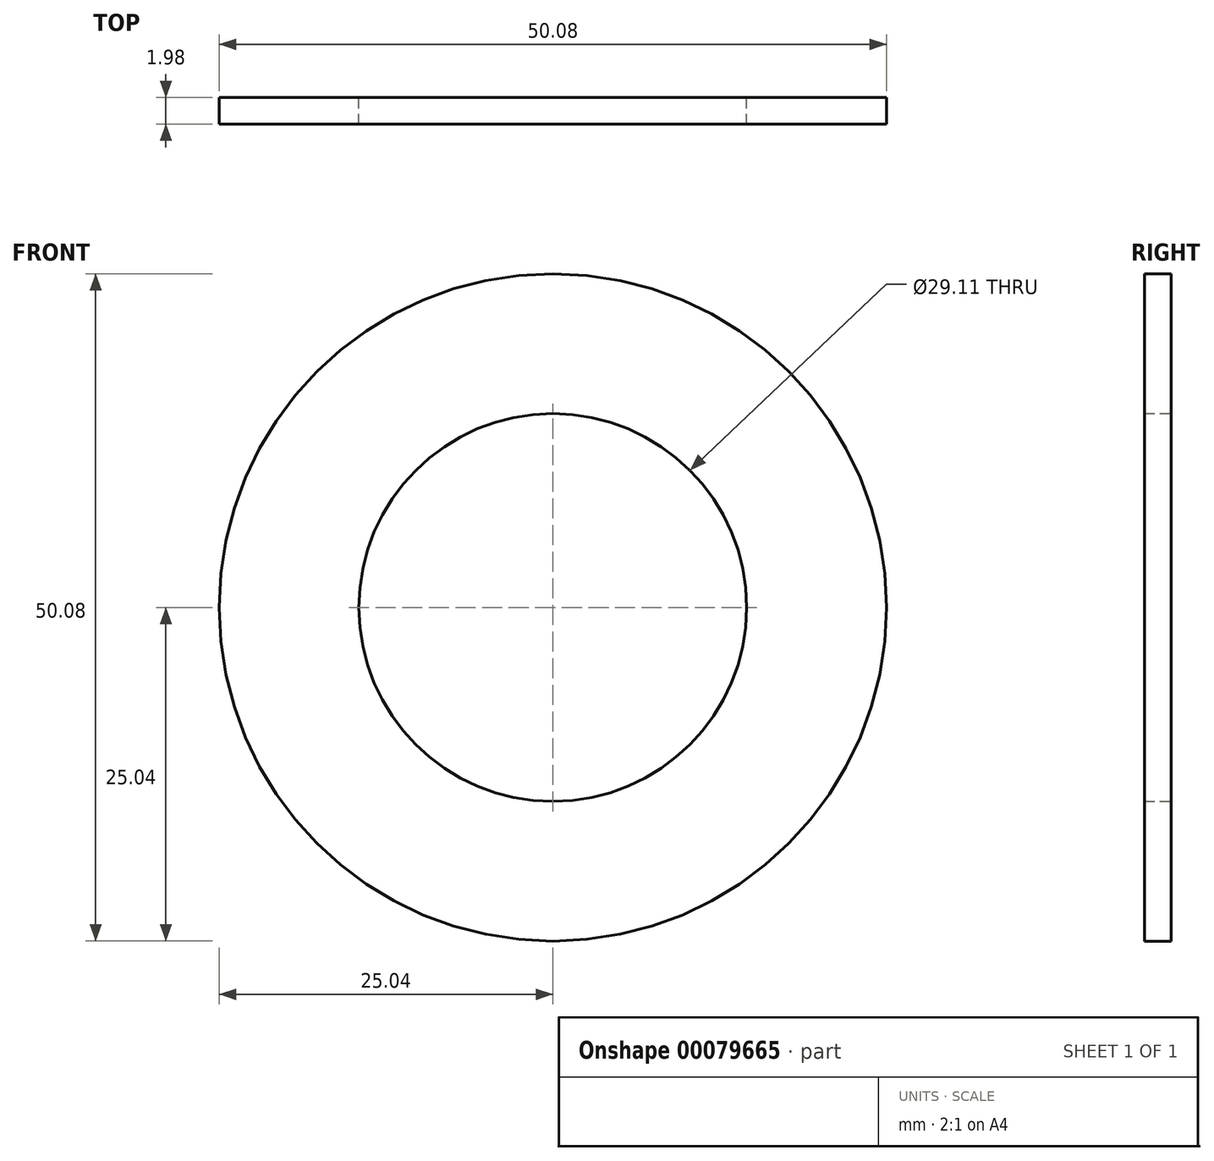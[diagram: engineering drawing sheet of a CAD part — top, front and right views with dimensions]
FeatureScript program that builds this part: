
annotation { "Feature Type Name" : "Feature", "Feature Type Description" : "" }
export const myFeature = defineFeature(function(context is Context, id is Id, definition is map)
    precondition{}
    {
        {
            var Q0;
            Q0=qCreatedBy(makeId("Front.planeOp"),FACE);
            var sketch = newSketch(context, id + "F0", { "sketchPlane" : qUnion([Q0])});
            skCircle(sketch, "E0", {"center": v(0, 0) * mm, "radius": 25.04 * mm});
            skCircle(sketch, "E1", {"center": v(0, 0) * mm, "radius": 14.55 * mm});
            skSolve(sketch);
        }
        {
            var Q0;
            Q0=makeQuery(id+"F0.imprint","IMPRINT",FACE,{"disambiguationData":[TD([[makeQuery(id+"F0.imprint","IMPRINT",EDGE,{"derivedFrom":sQuery(id+"F0.wireOp",EDGE,"E0")}),1.0]])]});
            extrude(context, id + "F1", {"entities" : qUnion([Q0]), "depth" : 1.98 * mm});
        }
    });
